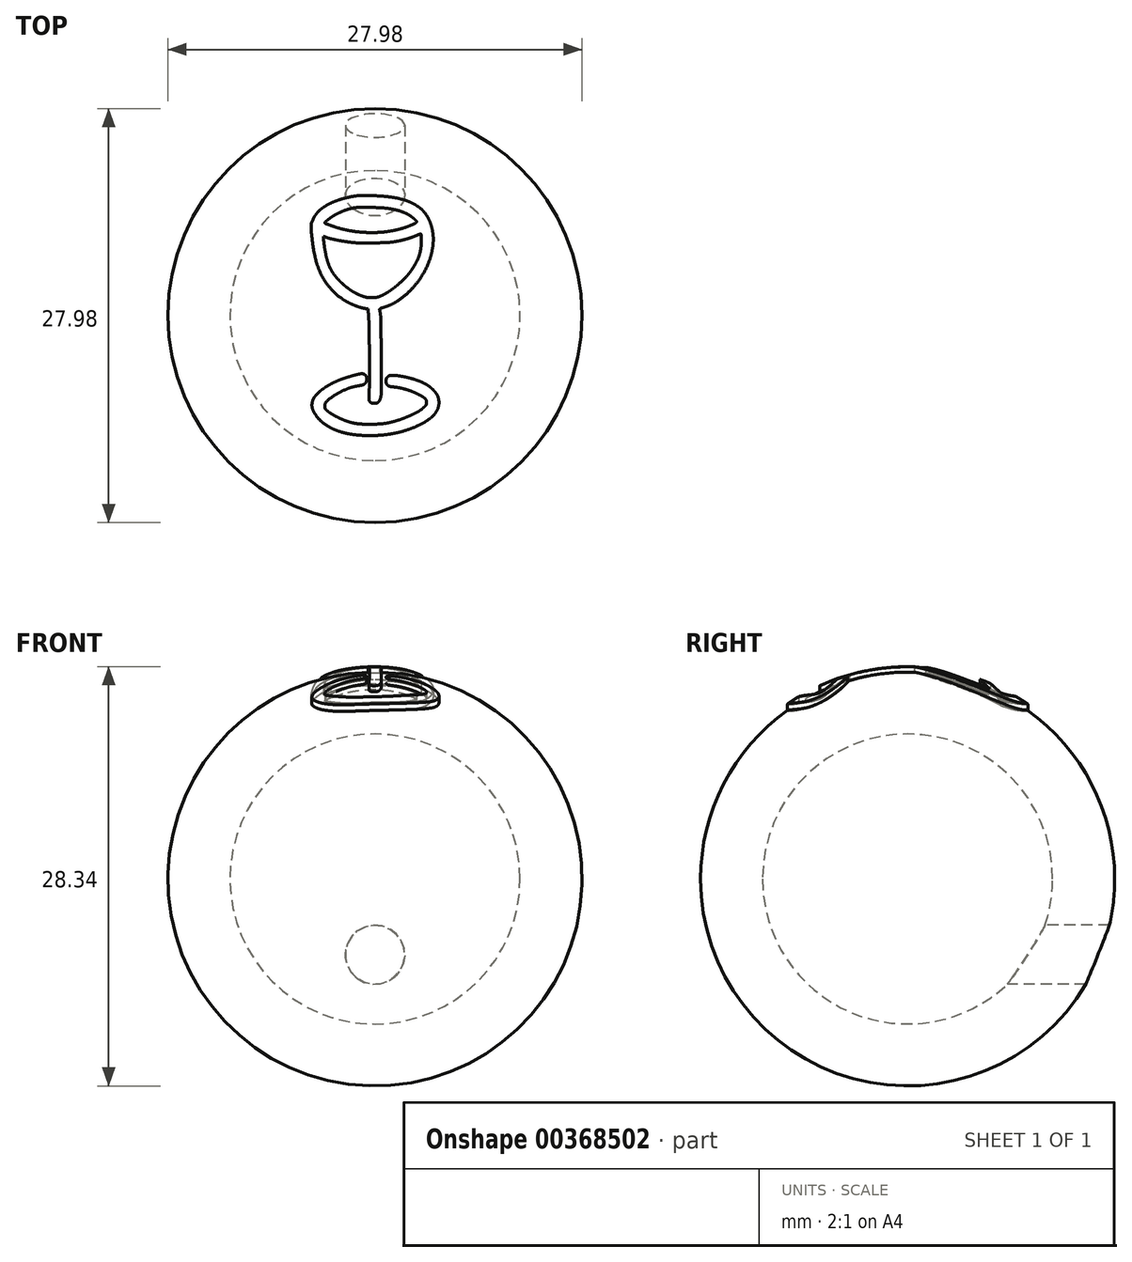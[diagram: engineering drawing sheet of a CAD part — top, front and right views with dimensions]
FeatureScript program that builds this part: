
annotation { "Feature Type Name" : "Feature", "Feature Type Description" : "" }
export const myFeature = defineFeature(function(context is Context, id is Id, definition is map)
    precondition{}
    {
        {
            var Q0;
            Q0=qCreatedBy(makeId("Top.planeOp"),FACE);
            var sketch = newSketch(context, id + "F0", { "sketchPlane" : qUnion([Q0])});
            skLineSegment(sketch, "E0", {"start": v(0, -10) * mm, "end": v(0, 10) * mm});
            skArc(sketch, "E1", {"start": v(0, 10) * mm, "mid": v(-10, 0) * mm, "end": v(0, -10) * mm});
            skSolve(sketch);
        }
        {
            var Q0;
            {var subQ0=sQuery(id+"F0.wireOp",EDGE,"E1");Q0=makeQuery(id+"F0.imprint","IMPRINT",FACE,{"disambiguationData":[TD([[makeQuery(id+"F0.imprint","IMPRINT",EDGE,{"derivedFrom":subQ0}),1.0]])]});}
            var Q1;
            Q1=sQuery(id+"F0.wireOp",EDGE,"E0");
            revolve(context, id + "F1", {"entities" : qUnion([Q0]), "axis" : qUnion([Q1]), "revolveType" : RevolveType.FULL});
        }
        {
            var Q0;
            Q0=makeQuery(id+"F1.opRevolve","SWEPT_BODY",BODY,{"disambiguationData":[OSD([sQuery(id+"F0.wireOp",EDGE,"E0"),sQuery(id+"F0.wireOp",EDGE,"E1")])]});
            var Q1;
            Q1=sQuery(id+"F0.wireOp",VERTEX,"NPe4G0ez-t7S9-9isL-QO5v-uuJu600mHcIT.center");
            var Q2;
            Q2=sQuery(id+"F0.wireOp",VERTEX,"E1.center");
            transform(context, id + "F2", {"entities" : qUnion([Q0]), "transformType" : TransformType.SCALE_UNIFORMLY, "scale" : 33.3, "scalePoint" : qUnion([Q2]), "makeCopy" : false});
        }
        {
            var Q0;
            Q0=qCreatedBy(makeId("Top.planeOp"),FACE);
            var sketch = newSketch(context, id + "F3", { "sketchPlane" : qUnion([Q0])});
            skArc(sketch, "E2", {"start": v(-28, 192.81) * mm, "mid": v(-31.38, 192.4) * mm, "end": v(-34.76, 191.86) * mm});
            skArc(sketch, "E3", {"start": v(-34.76, 191.86) * mm, "mid": v(-38.6, 191.14) * mm, "end": v(-42.43, 190.34) * mm});
            skArc(sketch, "E4", {"start": v(-42.43, 190.34) * mm, "mid": v(-46.3, 189.44) * mm, "end": v(-50.14, 188.46) * mm});
            skArc(sketch, "E5", {"start": v(-50.14, 188.46) * mm, "mid": v(-53.62, 187.47) * mm, "end": v(-57.07, 186.38) * mm});
            skArc(sketch, "E6", {"start": v(-57.07, 186.38) * mm, "mid": v(-64.8, 183.56) * mm, "end": v(-72.35, 180.29) * mm});
            skArc(sketch, "E7", {"start": v(-72.35, 180.29) * mm, "mid": v(-78.57, 177) * mm, "end": v(-84.46, 173.13) * mm});
            skArc(sketch, "E8", {"start": v(-84.46, 173.13) * mm, "mid": v(-89.14, 169.3) * mm, "end": v(-93.37, 164.97) * mm});
            skArc(sketch, "E9", {"start": v(-93.37, 164.97) * mm, "mid": v(-96.59, 160.63) * mm, "end": v(-99.08, 155.83) * mm});
            skArc(sketch, "E10", {"start": v(-99.08, 155.83) * mm, "mid": v(-99.5, 154.83) * mm, "end": v(-99.94, 153.82) * mm});
            skArc(sketch, "E11", {"start": v(-99.94, 153.82) * mm, "mid": v(-100.4, 152.79) * mm, "end": v(-100.85, 151.75) * mm});
            skArc(sketch, "E12", {"start": v(-100.85, 151.75) * mm, "mid": v(-101.26, 150.84) * mm, "end": v(-101.67, 149.92) * mm});
            skArc(sketch, "E13", {"start": v(-101.67, 149.92) * mm, "mid": v(-101.95, 149.32) * mm, "end": v(-102.24, 148.73) * mm});
            skArc(sketch, "E14", {"start": v(-102.24, 148.73) * mm, "mid": v(-102.57, 147.87) * mm, "end": v(-102.73, 146.96) * mm});
            skArc(sketch, "E15", {"start": v(-102.73, 146.96) * mm, "mid": v(-102.82, 145.41) * mm, "end": v(-102.85, 143.86) * mm});
            skArc(sketch, "E16", {"start": v(-102.85, 143.86) * mm, "mid": v(-102.8, 141.6) * mm, "end": v(-102.69, 139.34) * mm});
            skArc(sketch, "E17", {"start": v(-102.69, 139.34) * mm, "mid": v(-102.44, 135.94) * mm, "end": v(-102.17, 132.54) * mm});
            skArc(sketch, "E18", {"start": v(-102.17, 132.54) * mm, "mid": v(-100.04, 114.16) * mm, "end": v(-96.8, 95.94) * mm});
            skArc(sketch, "E19", {"start": v(-96.8, 95.94) * mm, "mid": v(-92.94, 81.56) * mm, "end": v(-87.47, 67.71) * mm});
            skArc(sketch, "E20", {"start": v(-87.47, 67.71) * mm, "mid": v(-81.13, 56.12) * mm, "end": v(-73.3, 45.49) * mm});
            skArc(sketch, "E21", {"start": v(-73.3, 45.49) * mm, "mid": v(-63.92, 35.71) * mm, "end": v(-53.4, 27.18) * mm});
            skArc(sketch, "E22", {"start": v(-53.4, 27.18) * mm, "mid": v(-49.24, 24.41) * mm, "end": v(-44.9, 21.92) * mm});
            skArc(sketch, "E23", {"start": v(-44.9, 21.92) * mm, "mid": v(-39.88, 19.4) * mm, "end": v(-34.74, 17.1) * mm});
            skArc(sketch, "E24", {"start": v(-34.74, 17.1) * mm, "mid": v(-29.55, 15.07) * mm, "end": v(-24.28, 13.28) * mm});
            skArc(sketch, "E25", {"start": v(-24.28, 13.28) * mm, "mid": v(-19.62, 12) * mm, "end": v(-14.89, 11.06) * mm});
            skLineSegment(sketch, "E26", {"start": v(-14.89, 11.06) * mm, "end": v(-11.28, 10.47) * mm});
            skLineSegment(sketch, "E27", {"start": v(-11.28, 10.47) * mm, "end": v(-10.56, 2.24) * mm});
            skArc(sketch, "E28", {"start": v(-10.56, 2.24) * mm, "mid": v(-9.95, -6.44) * mm, "end": v(-9.64, -15.14) * mm});
            skArc(sketch, "E29", {"start": v(-9.64, -15.14) * mm, "mid": v(-9.3, -35.9) * mm, "end": v(-9.02, -56.67) * mm});
            skArc(sketch, "E30", {"start": v(-9.02, -56.67) * mm, "mid": v(-8.82, -77.32) * mm, "end": v(-8.7, -97.97) * mm});
            skArc(sketch, "E31", {"start": v(-8.7, -97.97) * mm, "mid": v(-8.8, -108.17) * mm, "end": v(-9.18, -118.37) * mm});
            skArc(sketch, "E32", {"start": v(-9.18, -118.37) * mm, "mid": v(-9.47, -124.4) * mm, "end": v(-9.74, -130.44) * mm});
            skArc(sketch, "E33", {"start": v(-9.74, -130.44) * mm, "mid": v(-9.78, -132.57) * mm, "end": v(-9.7, -134.7) * mm});
            skArc(sketch, "E34", {"start": v(-9.7, -134.7) * mm, "mid": v(-9.52, -135.94) * mm, "end": v(-9.15, -137.13) * mm});
            skArc(sketch, "E35", {"start": v(-9.15, -137.13) * mm, "mid": v(-8.6, -138.18) * mm, "end": v(-7.87, -139.12) * mm});
            skArc(sketch, "E36", {"start": v(-7.87, -139.12) * mm, "mid": v(-7.27, -139.7) * mm, "end": v(-6.62, -140.22) * mm});
            skArc(sketch, "E37", {"start": v(-6.62, -140.22) * mm, "mid": v(-5.96, -140.63) * mm, "end": v(-5.26, -140.95) * mm});
            skArc(sketch, "E38", {"start": v(-5.26, -140.95) * mm, "mid": v(-4.48, -141.2) * mm, "end": v(-3.68, -141.36) * mm});
            skArc(sketch, "E39", {"start": v(-3.68, -141.36) * mm, "mid": v(-2.72, -141.46) * mm, "end": v(-1.75, -141.5) * mm});
            skArc(sketch, "E40", {"start": v(-1.75, -141.5) * mm, "mid": v(0, -141.42) * mm, "end": v(1.72, -141.18) * mm});
            skArc(sketch, "E41", {"start": v(1.72, -141.18) * mm, "mid": v(3.04, -140.82) * mm, "end": v(4.26, -140.22) * mm});
            skArc(sketch, "E42", {"start": v(4.26, -140.22) * mm, "mid": v(5.31, -139.43) * mm, "end": v(6.2, -138.45) * mm});
            skArc(sketch, "E43", {"start": v(6.2, -138.45) * mm, "mid": v(7.08, -137.1) * mm, "end": v(7.82, -135.66) * mm});
            skArc(sketch, "E44", {"start": v(7.82, -135.66) * mm, "mid": v(9.39, -130.88) * mm, "end": v(9.93, -125.87) * mm});
            skArc(sketch, "E45", {"start": v(9.93, -125.87) * mm, "mid": v(9.97, -95.78) * mm, "end": v(9.93, -65.68) * mm});
            skArc(sketch, "E46", {"start": v(9.93, -65.68) * mm, "mid": v(9.77, -36.7) * mm, "end": v(9.47, -7.73) * mm});
            skArc(sketch, "E47", {"start": v(9.47, -7.73) * mm, "mid": v(8.9, 0.7) * mm, "end": v(7.4, 9) * mm});
            skArc(sketch, "E48", {"start": v(7.4, 9) * mm, "mid": v(7.35, 9.57) * mm, "end": v(7.47, 10.13) * mm});
            skArc(sketch, "E49", {"start": v(7.47, 10.13) * mm, "mid": v(7.75, 10.61) * mm, "end": v(8.17, 10.99) * mm});
            skArc(sketch, "E50", {"start": v(8.17, 10.99) * mm, "mid": v(8.98, 11.43) * mm, "end": v(9.85, 11.77) * mm});
            skArc(sketch, "E51", {"start": v(9.85, 11.77) * mm, "mid": v(11.67, 12.35) * mm, "end": v(13.5, 12.9) * mm});
            skArc(sketch, "E52", {"start": v(13.5, 12.9) * mm, "mid": v(25.53, 17.38) * mm, "end": v(36.7, 23.67) * mm});
            skArc(sketch, "E53", {"start": v(36.7, 23.67) * mm, "mid": v(48.2, 32.34) * mm, "end": v(58.64, 42.23) * mm});
            skArc(sketch, "E54", {"start": v(58.64, 42.23) * mm, "mid": v(68.36, 53.67) * mm, "end": v(76.8, 66.08) * mm});
            skArc(sketch, "E55", {"start": v(76.8, 66.08) * mm, "mid": v(83.57, 78.94) * mm, "end": v(88.8, 92.5) * mm});
            skArc(sketch, "E56", {"start": v(88.8, 92.5) * mm, "mid": v(91.23, 101.41) * mm, "end": v(92.9, 110.5) * mm});
            skArc(sketch, "E57", {"start": v(92.9, 110.5) * mm, "mid": v(93.67, 119.1) * mm, "end": v(93.55, 127.73) * mm});
            skArc(sketch, "E58", {"start": v(93.55, 127.73) * mm, "mid": v(92.56, 135.93) * mm, "end": v(90.68, 143.97) * mm});
            skArc(sketch, "E59", {"start": v(90.68, 143.97) * mm, "mid": v(87.96, 151.66) * mm, "end": v(84.4, 159) * mm});
            skArc(sketch, "E60", {"start": v(84.4, 159) * mm, "mid": v(80.6, 164.75) * mm, "end": v(75.97, 169.86) * mm});
            skArc(sketch, "E61", {"start": v(75.97, 169.86) * mm, "mid": v(70.26, 174.63) * mm, "end": v(64.02, 178.68) * mm});
            skArc(sketch, "E62", {"start": v(64.02, 178.68) * mm, "mid": v(56.48, 182.45) * mm, "end": v(48.6, 185.4) * mm});
            skArc(sketch, "E63", {"start": v(48.6, 185.4) * mm, "mid": v(39.26, 188) * mm, "end": v(29.76, 189.95) * mm});
            skArc(sketch, "E64", {"start": v(29.76, 189.95) * mm, "mid": v(23.24, 190.92) * mm, "end": v(16.69, 191.62) * mm});
            skArc(sketch, "E65", {"start": v(16.69, 191.62) * mm, "mid": v(8.13, 192.28) * mm, "end": v(-0.44, 192.79) * mm});
            skArc(sketch, "E66", {"start": v(-0.44, 192.79) * mm, "mid": v(-8.76, 193.13) * mm, "end": v(-17.1, 193.32) * mm});
            skArc(sketch, "E67", {"start": v(-17.1, 193.32) * mm, "mid": v(-22.55, 193.23) * mm, "end": v(-28, 192.81) * mm});
            skArc(sketch, "E68", {"start": v(23, 172) * mm, "mid": v(27.27, 171.24) * mm, "end": v(31.52, 170.4) * mm});
            skArc(sketch, "E69", {"start": v(31.52, 170.4) * mm, "mid": v(34.9, 169.63) * mm, "end": v(38.25, 168.73) * mm});
            skArc(sketch, "E70", {"start": v(38.25, 168.73) * mm, "mid": v(41.28, 167.77) * mm, "end": v(44.27, 166.68) * mm});
            skArc(sketch, "E71", {"start": v(44.27, 166.68) * mm, "mid": v(47.43, 165.38) * mm, "end": v(50.56, 163.97) * mm});
            skArc(sketch, "E72", {"start": v(50.56, 163.97) * mm, "mid": v(53.44, 162.47) * mm, "end": v(56.2, 160.78) * mm});
            skArc(sketch, "E73", {"start": v(56.2, 160.78) * mm, "mid": v(59.05, 158.78) * mm, "end": v(61.78, 156.62) * mm});
            skArc(sketch, "E74", {"start": v(61.78, 156.62) * mm, "mid": v(64.08, 154.6) * mm, "end": v(66.28, 152.48) * mm});
            skArc(sketch, "E75", {"start": v(66.28, 152.48) * mm, "mid": v(66.84, 151.48) * mm, "end": v(66.79, 150.33) * mm});
            skArc(sketch, "E76", {"start": v(66.79, 150.33) * mm, "mid": v(66.12, 149.19) * mm, "end": v(65.05, 148.41) * mm});
            skArc(sketch, "E77", {"start": v(65.05, 148.41) * mm, "mid": v(60.8, 146.55) * mm, "end": v(56.5, 144.76) * mm});
            skArc(sketch, "E78", {"start": v(56.5, 144.76) * mm, "mid": v(51.74, 142.91) * mm, "end": v(46.93, 141.22) * mm});
            skArc(sketch, "E79", {"start": v(46.93, 141.22) * mm, "mid": v(42.34, 139.79) * mm, "end": v(37.7, 138.53) * mm});
            skArc(sketch, "E80", {"start": v(37.7, 138.53) * mm, "mid": v(24.83, 135.84) * mm, "end": v(11.79, 134.2) * mm});
            skArc(sketch, "E81", {"start": v(11.79, 134.2) * mm, "mid": v(-2.07, 133.48) * mm, "end": v(-15.94, 133.71) * mm});
            skArc(sketch, "E82", {"start": v(-15.94, 133.71) * mm, "mid": v(-29.73, 134.9) * mm, "end": v(-43.4, 137.01) * mm});
            skArc(sketch, "E83", {"start": v(-43.4, 137.01) * mm, "mid": v(-56.09, 139.97) * mm, "end": v(-68.5, 143.96) * mm});
            skArc(sketch, "E84", {"start": v(-68.5, 143.96) * mm, "mid": v(-70.45, 144.68) * mm, "end": v(-72.41, 145.4) * mm});
            skArc(sketch, "E85", {"start": v(-72.41, 145.4) * mm, "mid": v(-74.17, 146.03) * mm, "end": v(-75.92, 146.67) * mm});
            skArc(sketch, "E86", {"start": v(-75.92, 146.67) * mm, "mid": v(-77.4, 147.2) * mm, "end": v(-78.88, 147.74) * mm});
            skArc(sketch, "E87", {"start": v(-78.88, 147.74) * mm, "mid": v(-79.3, 147.9) * mm, "end": v(-79.74, 148.04) * mm});
            skArc(sketch, "E88", {"start": v(-79.74, 148.04) * mm, "mid": v(-80.25, 148.32) * mm, "end": v(-80.62, 148.77) * mm});
            skArc(sketch, "E89", {"start": v(-80.62, 148.77) * mm, "mid": v(-80.74, 149.28) * mm, "end": v(-80.58, 149.77) * mm});
            skArc(sketch, "E90", {"start": v(-80.58, 149.77) * mm, "mid": v(-79.94, 150.6) * mm, "end": v(-79.2, 151.33) * mm});
            skArc(sketch, "E91", {"start": v(-79.2, 151.33) * mm, "mid": v(-77.48, 152.74) * mm, "end": v(-75.74, 154.13) * mm});
            skArc(sketch, "E92", {"start": v(-75.74, 154.13) * mm, "mid": v(-70.76, 157.76) * mm, "end": v(-65.57, 161.08) * mm});
            skArc(sketch, "E93", {"start": v(-65.57, 161.08) * mm, "mid": v(-60.08, 164.12) * mm, "end": v(-54.43, 166.82) * mm});
            skArc(sketch, "E94", {"start": v(-54.43, 166.82) * mm, "mid": v(-48.77, 169.12) * mm, "end": v(-43, 171.06) * mm});
            skArc(sketch, "E95", {"start": v(-43, 171.06) * mm, "mid": v(-37.5, 172.49) * mm, "end": v(-31.93, 173.5) * mm});
            skArc(sketch, "E96", {"start": v(-31.93, 173.5) * mm, "mid": v(-27.17, 174) * mm, "end": v(-22.38, 174.16) * mm});
            skArc(sketch, "E97", {"start": v(-22.38, 174.16) * mm, "mid": v(-13.79, 174.1) * mm, "end": v(-5.2, 173.93) * mm});
            skArc(sketch, "E98", {"start": v(-5.2, 173.93) * mm, "mid": v(3.46, 173.63) * mm, "end": v(12.1, 173.2) * mm});
            skArc(sketch, "E99", {"start": v(12.1, 173.2) * mm, "mid": v(17.57, 172.75) * mm, "end": v(23, 172) * mm});
            skArc(sketch, "E100", {"start": v(74.45, 118.91) * mm, "mid": v(74.2, 112.9) * mm, "end": v(73.54, 106.92) * mm});
            skArc(sketch, "E101", {"start": v(73.54, 106.92) * mm, "mid": v(72.47, 101.46) * mm, "end": v(70.92, 96.12) * mm});
            skArc(sketch, "E102", {"start": v(70.92, 96.12) * mm, "mid": v(68.79, 90.64) * mm, "end": v(66.2, 85.35) * mm});
            skArc(sketch, "E103", {"start": v(66.2, 85.35) * mm, "mid": v(62.73, 79.3) * mm, "end": v(58.94, 73.4) * mm});
            skArc(sketch, "E104", {"start": v(58.94, 73.4) * mm, "mid": v(54.72, 67.67) * mm, "end": v(50.07, 62.26) * mm});
            skArc(sketch, "E105", {"start": v(50.07, 62.26) * mm, "mid": v(44.37, 56.43) * mm, "end": v(38.38, 50.9) * mm});
            skArc(sketch, "E106", {"start": v(38.38, 50.9) * mm, "mid": v(32.1, 45.67) * mm, "end": v(25.56, 40.76) * mm});
            skArc(sketch, "E107", {"start": v(25.56, 40.76) * mm, "mid": v(19.56, 36.81) * mm, "end": v(13.27, 33.33) * mm});
            skArc(sketch, "E108", {"start": v(13.27, 33.33) * mm, "mid": v(10.86, 32.14) * mm, "end": v(8.43, 31.02) * mm});
            skArc(sketch, "E109", {"start": v(8.43, 31.02) * mm, "mid": v(6.75, 30.34) * mm, "end": v(5.03, 29.79) * mm});
            skArc(sketch, "E110", {"start": v(5.03, 29.79) * mm, "mid": v(3.33, 29.38) * mm, "end": v(1.6, 29.12) * mm});
            skArc(sketch, "E111", {"start": v(1.6, 29.12) * mm, "mid": v(-0.81, 28.88) * mm, "end": v(-3.23, 28.72) * mm});
            skArc(sketch, "E112", {"start": v(-3.23, 28.72) * mm, "mid": v(-5.59, 28.63) * mm, "end": v(-7.95, 28.6) * mm});
            skArc(sketch, "E113", {"start": v(-7.95, 28.6) * mm, "mid": v(-9.7, 28.66) * mm, "end": v(-11.43, 28.84) * mm});
            skArc(sketch, "E114", {"start": v(-11.43, 28.84) * mm, "mid": v(-13.15, 29.14) * mm, "end": v(-14.86, 29.55) * mm});
            skArc(sketch, "E115", {"start": v(-14.86, 29.55) * mm, "mid": v(-17.14, 30.22) * mm, "end": v(-19.4, 30.94) * mm});
            skArc(sketch, "E116", {"start": v(-19.4, 30.94) * mm, "mid": v(-24.3, 32.77) * mm, "end": v(-29.04, 34.94) * mm});
            skArc(sketch, "E117", {"start": v(-29.04, 34.94) * mm, "mid": v(-33.85, 37.5) * mm, "end": v(-38.48, 40.37) * mm});
            skArc(sketch, "E118", {"start": v(-38.48, 40.37) * mm, "mid": v(-43.29, 43.72) * mm, "end": v(-47.9, 47.34) * mm});
            skArc(sketch, "E119", {"start": v(-47.9, 47.34) * mm, "mid": v(-52.76, 51.57) * mm, "end": v(-57.44, 56) * mm});
            skArc(sketch, "E120", {"start": v(-57.44, 56) * mm, "mid": v(-62.23, 61.17) * mm, "end": v(-66.53, 66.76) * mm});
            skArc(sketch, "E121", {"start": v(-66.53, 66.76) * mm, "mid": v(-70.15, 72.57) * mm, "end": v(-73.17, 78.7) * mm});
            skArc(sketch, "E122", {"start": v(-73.17, 78.7) * mm, "mid": v(-75.9, 85.84) * mm, "end": v(-77.98, 93.19) * mm});
            skArc(sketch, "E123", {"start": v(-77.98, 93.19) * mm, "mid": v(-79.95, 102.45) * mm, "end": v(-81.5, 111.79) * mm});
            skArc(sketch, "E124", {"start": v(-81.5, 111.79) * mm, "mid": v(-81.79, 113.84) * mm, "end": v(-82.06, 115.9) * mm});
            skArc(sketch, "E125", {"start": v(-82.06, 115.9) * mm, "mid": v(-82.3, 117.84) * mm, "end": v(-82.53, 119.8) * mm});
            skArc(sketch, "E126", {"start": v(-82.53, 119.8) * mm, "mid": v(-82.72, 121.44) * mm, "end": v(-82.89, 123.1) * mm});
            skArc(sketch, "E127", {"start": v(-82.89, 123.1) * mm, "mid": v(-82.95, 123.9) * mm, "end": v(-82.97, 124.7) * mm});
            skLineSegment(sketch, "E128", {"start": v(-82.97, 124.7) * mm, "end": v(-83, 127.4) * mm});
            skLineSegment(sketch, "E129", {"start": v(-83, 127.4) * mm, "end": v(-77.24, 125.41) * mm});
            skArc(sketch, "E130", {"start": v(-77.24, 125.41) * mm, "mid": v(-73.46, 124.22) * mm, "end": v(-69.61, 123.22) * mm});
            skArc(sketch, "E131", {"start": v(-69.61, 123.22) * mm, "mid": v(-64.09, 122) * mm, "end": v(-58.54, 120.88) * mm});
            skArc(sketch, "E132", {"start": v(-58.54, 120.88) * mm, "mid": v(-52.55, 119.8) * mm, "end": v(-46.55, 118.82) * mm});
            skArc(sketch, "E133", {"start": v(-46.55, 118.82) * mm, "mid": v(-41.1, 118.06) * mm, "end": v(-35.66, 117.44) * mm});
            skArc(sketch, "E134", {"start": v(-35.66, 117.44) * mm, "mid": v(-28.26, 116.87) * mm, "end": v(-20.84, 116.63) * mm});
            skArc(sketch, "E135", {"start": v(-20.84, 116.63) * mm, "mid": v(-10.4, 116.6) * mm, "end": v(0.05, 116.76) * mm});
            skArc(sketch, "E136", {"start": v(0.05, 116.76) * mm, "mid": v(10.3, 117.07) * mm, "end": v(20.54, 117.54) * mm});
            skArc(sketch, "E137", {"start": v(20.54, 117.54) * mm, "mid": v(26.8, 118.08) * mm, "end": v(33, 119) * mm});
            skArc(sketch, "E138", {"start": v(33, 119) * mm, "mid": v(37.48, 119.88) * mm, "end": v(41.92, 120.86) * mm});
            skArc(sketch, "E139", {"start": v(41.92, 120.86) * mm, "mid": v(46.33, 121.94) * mm, "end": v(50.71, 123.15) * mm});
            skArc(sketch, "E140", {"start": v(50.71, 123.15) * mm, "mid": v(54.81, 124.38) * mm, "end": v(58.87, 125.73) * mm});
            skArc(sketch, "E141", {"start": v(58.87, 125.73) * mm, "mid": v(62.4, 127.02) * mm, "end": v(65.87, 128.45) * mm});
            skArc(sketch, "E142", {"start": v(65.87, 128.45) * mm, "mid": v(67.17, 129.01) * mm, "end": v(68.48, 129.54) * mm});
            skArc(sketch, "E143", {"start": v(68.48, 129.54) * mm, "mid": v(69.66, 130) * mm, "end": v(70.85, 130.42) * mm});
            skArc(sketch, "E144", {"start": v(70.85, 130.42) * mm, "mid": v(71.84, 130.75) * mm, "end": v(72.84, 131.07) * mm});
            skArc(sketch, "E145", {"start": v(72.84, 131.07) * mm, "mid": v(73.17, 131.13) * mm, "end": v(73.5, 131.09) * mm});
            skArc(sketch, "E146", {"start": v(73.5, 131.09) * mm, "mid": v(73.8, 130.9) * mm, "end": v(73.94, 130.6) * mm});
            skArc(sketch, "E147", {"start": v(73.94, 130.6) * mm, "mid": v(74.09, 129.1) * mm, "end": v(74.22, 127.62) * mm});
            skArc(sketch, "E148", {"start": v(74.22, 127.62) * mm, "mid": v(74.34, 125.7) * mm, "end": v(74.4, 123.79) * mm});
            skArc(sketch, "E149", {"start": v(74.4, 123.79) * mm, "mid": v(74.45, 121.35) * mm, "end": v(74.45, 118.91) * mm});
            skArc(sketch, "E150", {"start": v(-34.65, -96.5) * mm, "mid": v(-43.47, -99) * mm, "end": v(-52.16, -101.92) * mm});
            skArc(sketch, "E151", {"start": v(-52.16, -101.92) * mm, "mid": v(-60, -105) * mm, "end": v(-67.65, -108.52) * mm});
            skArc(sketch, "E152", {"start": v(-67.65, -108.52) * mm, "mid": v(-74.33, -112.1) * mm, "end": v(-80.77, -116.1) * mm});
            skArc(sketch, "E153", {"start": v(-80.77, -116.1) * mm, "mid": v(-86.14, -120.06) * mm, "end": v(-91.13, -124.5) * mm});
            skArc(sketch, "E154", {"start": v(-91.13, -124.5) * mm, "mid": v(-93.26, -126.63) * mm, "end": v(-95.35, -128.8) * mm});
            skArc(sketch, "E155", {"start": v(-95.35, -128.8) * mm, "mid": v(-96.6, -130.2) * mm, "end": v(-97.73, -131.7) * mm});
            skArc(sketch, "E156", {"start": v(-97.73, -131.7) * mm, "mid": v(-98.56, -133.01) * mm, "end": v(-99.25, -134.4) * mm});
            skArc(sketch, "E157", {"start": v(-99.25, -134.4) * mm, "mid": v(-99.92, -136.08) * mm, "end": v(-100.48, -137.8) * mm});
            skArc(sketch, "E158", {"start": v(-100.48, -137.8) * mm, "mid": v(-101.1, -140.5) * mm, "end": v(-101.43, -143.24) * mm});
            skArc(sketch, "E159", {"start": v(-101.43, -143.24) * mm, "mid": v(-101.41, -145.8) * mm, "end": v(-101.04, -148.34) * mm});
            skArc(sketch, "E160", {"start": v(-101.04, -148.34) * mm, "mid": v(-100.3, -151.03) * mm, "end": v(-99.22, -153.6) * mm});
            skArc(sketch, "E161", {"start": v(-99.22, -153.6) * mm, "mid": v(-97.61, -156.62) * mm, "end": v(-95.8, -159.53) * mm});
            skArc(sketch, "E162", {"start": v(-95.8, -159.53) * mm, "mid": v(-89.92, -166.94) * mm, "end": v(-82.9, -173.28) * mm});
            skArc(sketch, "E163", {"start": v(-82.9, -173.28) * mm, "mid": v(-74.32, -179.02) * mm, "end": v(-65.07, -183.62) * mm});
            skArc(sketch, "E164", {"start": v(-65.07, -183.62) * mm, "mid": v(-54.02, -187.58) * mm, "end": v(-42.6, -190.32) * mm});
            skArc(sketch, "E165", {"start": v(-42.6, -190.32) * mm, "mid": v(-29.29, -192.24) * mm, "end": v(-15.88, -193.2) * mm});
            skArc(sketch, "E166", {"start": v(-15.88, -193.2) * mm, "mid": v(-3.6, -193.28) * mm, "end": v(8.67, -192.7) * mm});
            skArc(sketch, "E167", {"start": v(8.67, -192.7) * mm, "mid": v(20.3, -191.45) * mm, "end": v(31.83, -189.47) * mm});
            skArc(sketch, "E168", {"start": v(31.83, -189.47) * mm, "mid": v(42.82, -186.85) * mm, "end": v(53.62, -183.51) * mm});
            skArc(sketch, "E169", {"start": v(53.62, -183.51) * mm, "mid": v(64, -179.52) * mm, "end": v(74.07, -174.83) * mm});
            skArc(sketch, "E170", {"start": v(74.07, -174.83) * mm, "mid": v(81.9, -170.36) * mm, "end": v(89.25, -165.16) * mm});
            skArc(sketch, "E171", {"start": v(89.25, -165.16) * mm, "mid": v(94.55, -160.17) * mm, "end": v(98.88, -154.31) * mm});
            skArc(sketch, "E172", {"start": v(98.88, -154.31) * mm, "mid": v(101.48, -148.67) * mm, "end": v(102.73, -142.58) * mm});
            skArc(sketch, "E173", {"start": v(102.73, -142.58) * mm, "mid": v(102.6, -136.36) * mm, "end": v(101.06, -130.32) * mm});
            skArc(sketch, "E174", {"start": v(101.06, -130.32) * mm, "mid": v(99.8, -127.56) * mm, "end": v(98.15, -125) * mm});
            skArc(sketch, "E175", {"start": v(98.15, -125) * mm, "mid": v(95.8, -122.07) * mm, "end": v(93.23, -119.32) * mm});
            skArc(sketch, "E176", {"start": v(93.23, -119.32) * mm, "mid": v(90.25, -116.55) * mm, "end": v(87.08, -114) * mm});
            skArc(sketch, "E177", {"start": v(87.08, -114) * mm, "mid": v(83.81, -111.76) * mm, "end": v(80.39, -109.77) * mm});
            skArc(sketch, "E178", {"start": v(80.39, -109.77) * mm, "mid": v(74.8, -107.06) * mm, "end": v(69.03, -104.76) * mm});
            skArc(sketch, "E179", {"start": v(69.03, -104.76) * mm, "mid": v(62.06, -102.45) * mm, "end": v(55, -100.46) * mm});
            skArc(sketch, "E180", {"start": v(55, -100.46) * mm, "mid": v(47.95, -98.8) * mm, "end": v(40.82, -97.46) * mm});
            skArc(sketch, "E181", {"start": v(40.82, -97.46) * mm, "mid": v(34.96, -96.74) * mm, "end": v(29.05, -96.5) * mm});
            skArc(sketch, "E182", {"start": v(29.05, -96.5) * mm, "mid": v(27.14, -96.52) * mm, "end": v(25.23, -96.58) * mm});
            skArc(sketch, "E183", {"start": v(25.23, -96.58) * mm, "mid": v(24.15, -96.7) * mm, "end": v(23.09, -96.93) * mm});
            skArc(sketch, "E184", {"start": v(23.09, -96.93) * mm, "mid": v(22.28, -97.24) * mm, "end": v(21.53, -97.68) * mm});
            skArc(sketch, "E185", {"start": v(21.53, -97.68) * mm, "mid": v(20.7, -98.32) * mm, "end": v(19.96, -99.05) * mm});
            skArc(sketch, "E186", {"start": v(19.96, -99.05) * mm, "mid": v(18.9, -100.41) * mm, "end": v(18.15, -101.96) * mm});
            skArc(sketch, "E187", {"start": v(18.15, -101.96) * mm, "mid": v(17.67, -103.68) * mm, "end": v(17.5, -105.46) * mm});
            skArc(sketch, "E188", {"start": v(17.5, -105.46) * mm, "mid": v(17.64, -107.23) * mm, "end": v(18.1, -108.95) * mm});
            skArc(sketch, "E189", {"start": v(18.1, -108.95) * mm, "mid": v(18.82, -110.48) * mm, "end": v(19.85, -111.83) * mm});
            skArc(sketch, "E190", {"start": v(19.85, -111.83) * mm, "mid": v(20.58, -112.51) * mm, "end": v(21.4, -113.1) * mm});
            skArc(sketch, "E191", {"start": v(21.4, -113.1) * mm, "mid": v(22.26, -113.58) * mm, "end": v(23.18, -113.94) * mm});
            skArc(sketch, "E192", {"start": v(23.18, -113.94) * mm, "mid": v(24.43, -114.28) * mm, "end": v(25.7, -114.51) * mm});
            skArc(sketch, "E193", {"start": v(25.7, -114.51) * mm, "mid": v(27.76, -114.77) * mm, "end": v(29.83, -114.99) * mm});
            skArc(sketch, "E194", {"start": v(29.83, -114.99) * mm, "mid": v(34.38, -115.52) * mm, "end": v(38.9, -116.3) * mm});
            skArc(sketch, "E195", {"start": v(38.9, -116.3) * mm, "mid": v(43.66, -117.33) * mm, "end": v(48.37, -118.56) * mm});
            skArc(sketch, "E196", {"start": v(48.37, -118.56) * mm, "mid": v(53.13, -120.02) * mm, "end": v(57.83, -121.68) * mm});
            skArc(sketch, "E197", {"start": v(57.83, -121.68) * mm, "mid": v(62.38, -123.5) * mm, "end": v(66.85, -125.51) * mm});
            skArc(sketch, "E198", {"start": v(66.85, -125.51) * mm, "mid": v(71.1, -127.61) * mm, "end": v(75.29, -129.81) * mm});
            skArc(sketch, "E199", {"start": v(75.29, -129.81) * mm, "mid": v(77.66, -131.27) * mm, "end": v(79.85, -133) * mm});
            skArc(sketch, "E200", {"start": v(79.85, -133) * mm, "mid": v(81.17, -134.41) * mm, "end": v(82.18, -136.07) * mm});
            skArc(sketch, "E201", {"start": v(82.18, -136.07) * mm, "mid": v(82.8, -137.85) * mm, "end": v(83, -139.72) * mm});
            skArc(sketch, "E202", {"start": v(83, -139.72) * mm, "mid": v(82.96, -140.83) * mm, "end": v(82.8, -141.93) * mm});
            skArc(sketch, "E203", {"start": v(82.8, -141.93) * mm, "mid": v(82.56, -142.82) * mm, "end": v(82.18, -143.67) * mm});
            skArc(sketch, "E204", {"start": v(82.18, -143.67) * mm, "mid": v(81.6, -144.6) * mm, "end": v(80.91, -145.45) * mm});
            skArc(sketch, "E205", {"start": v(80.91, -145.45) * mm, "mid": v(79.73, -146.72) * mm, "end": v(78.5, -147.95) * mm});
            skArc(sketch, "E206", {"start": v(78.5, -147.95) * mm, "mid": v(74.22, -151.58) * mm, "end": v(69.49, -154.6) * mm});
            skArc(sketch, "E207", {"start": v(69.49, -154.6) * mm, "mid": v(62.23, -158.37) * mm, "end": v(54.81, -161.8) * mm});
            skArc(sketch, "E208", {"start": v(54.81, -161.8) * mm, "mid": v(46.47, -165.2) * mm, "end": v(37.99, -168.23) * mm});
            skArc(sketch, "E209", {"start": v(37.99, -168.23) * mm, "mid": v(29.88, -170.67) * mm, "end": v(21.66, -172.67) * mm});
            skArc(sketch, "E210", {"start": v(21.66, -172.67) * mm, "mid": v(15.6, -173.75) * mm, "end": v(9.47, -174.4) * mm});
            skArc(sketch, "E211", {"start": v(9.47, -174.4) * mm, "mid": v(1.44, -174.86) * mm, "end": v(-6.6, -175.06) * mm});
            skArc(sketch, "E212", {"start": v(-6.6, -175.06) * mm, "mid": v(-14.57, -175) * mm, "end": v(-22.52, -174.7) * mm});
            skArc(sketch, "E213", {"start": v(-22.52, -174.7) * mm, "mid": v(-28.28, -174.16) * mm, "end": v(-33.98, -173.17) * mm});
            skArc(sketch, "E214", {"start": v(-33.98, -173.17) * mm, "mid": v(-42.09, -171.07) * mm, "end": v(-50, -168.32) * mm});
            skArc(sketch, "E215", {"start": v(-50, -168.32) * mm, "mid": v(-57.95, -164.86) * mm, "end": v(-65.6, -160.83) * mm});
            skArc(sketch, "E216", {"start": v(-65.6, -160.83) * mm, "mid": v(-71.87, -156.93) * mm, "end": v(-77.84, -152.6) * mm});
            skArc(sketch, "E217", {"start": v(-77.84, -152.6) * mm, "mid": v(-80.16, -149.75) * mm, "end": v(-81, -146.16) * mm});
            skArc(sketch, "E218", {"start": v(-81, -146.16) * mm, "mid": v(-79.94, -141.3) * mm, "end": v(-76.96, -137.33) * mm});
            skArc(sketch, "E219", {"start": v(-76.96, -137.33) * mm, "mid": v(-70, -131.79) * mm, "end": v(-62.58, -126.88) * mm});
            skArc(sketch, "E220", {"start": v(-62.58, -126.88) * mm, "mid": v(-53.6, -121.99) * mm, "end": v(-44.23, -117.89) * mm});
            skArc(sketch, "E221", {"start": v(-44.23, -117.89) * mm, "mid": v(-35.24, -114.97) * mm, "end": v(-26, -113.05) * mm});
            skArc(sketch, "E222", {"start": v(-26, -113.05) * mm, "mid": v(-23.72, -112.66) * mm, "end": v(-21.46, -112.16) * mm});
            skArc(sketch, "E223", {"start": v(-21.46, -112.16) * mm, "mid": v(-19.83, -111.67) * mm, "end": v(-18.26, -111) * mm});
            skArc(sketch, "E224", {"start": v(-18.26, -111) * mm, "mid": v(-17.07, -110.31) * mm, "end": v(-16, -109.46) * mm});
            skArc(sketch, "E225", {"start": v(-16, -109.46) * mm, "mid": v(-15.14, -108.5) * mm, "end": v(-14.44, -107.4) * mm});
            skArc(sketch, "E226", {"start": v(-14.44, -107.4) * mm, "mid": v(-13.76, -105.86) * mm, "end": v(-13.28, -104.24) * mm});
            skArc(sketch, "E227", {"start": v(-13.28, -104.24) * mm, "mid": v(-13.05, -102.7) * mm, "end": v(-13.06, -101.14) * mm});
            skArc(sketch, "E228", {"start": v(-13.06, -101.14) * mm, "mid": v(-13.3, -99.7) * mm, "end": v(-13.8, -98.31) * mm});
            skArc(sketch, "E229", {"start": v(-13.8, -98.31) * mm, "mid": v(-14.52, -97.06) * mm, "end": v(-15.45, -95.95) * mm});
            skArc(sketch, "E230", {"start": v(-15.45, -95.95) * mm, "mid": v(-16.65, -94.96) * mm, "end": v(-18.03, -94.24) * mm});
            skArc(sketch, "E231", {"start": v(-18.03, -94.24) * mm, "mid": v(-19.5, -93.8) * mm, "end": v(-21.04, -93.7) * mm});
            skArc(sketch, "E232", {"start": v(-21.04, -93.7) * mm, "mid": v(-23.35, -93.87) * mm, "end": v(-25.63, -94.28) * mm});
            skArc(sketch, "E233", {"start": v(-25.63, -94.28) * mm, "mid": v(-30.15, -95.35) * mm, "end": v(-34.65, -96.5) * mm});
            skArc(sketch, "E234", {"start": v(46.5, 109.42) * mm, "mid": v(40.62, 107.91) * mm, "end": v(34.69, 106.57) * mm});
            skArc(sketch, "E235", {"start": v(34.69, 106.57) * mm, "mid": v(29.15, 105.5) * mm, "end": v(23.57, 104.64) * mm});
            skArc(sketch, "E236", {"start": v(23.57, 104.64) * mm, "mid": v(17.7, 103.94) * mm, "end": v(11.79, 103.43) * mm});
            skArc(sketch, "E237", {"start": v(11.79, 103.43) * mm, "mid": v(4.84, 103.03) * mm, "end": v(-2.12, 102.78) * mm});
            skArc(sketch, "E238", {"start": v(-2.12, 102.78) * mm, "mid": v(-9.27, 102.65) * mm, "end": v(-16.41, 102.65) * mm});
            skArc(sketch, "E239", {"start": v(-16.41, 102.65) * mm, "mid": v(-22.2, 102.8) * mm, "end": v(-28, 103.15) * mm});
            skArc(sketch, "E240", {"start": v(-28, 103.15) * mm, "mid": v(-33.66, 103.68) * mm, "end": v(-39.3, 104.4) * mm});
            skArc(sketch, "E241", {"start": v(-39.3, 104.4) * mm, "mid": v(-46.04, 105.44) * mm, "end": v(-52.75, 106.63) * mm});
            skArc(sketch, "E242", {"start": v(-52.75, 106.63) * mm, "mid": v(-56.1, 107.24) * mm, "end": v(-59.46, 107.82) * mm});
            skArc(sketch, "E243", {"start": v(-59.46, 107.82) * mm, "mid": v(-61.02, 108.03) * mm, "end": v(-62.6, 108.15) * mm});
            skArc(sketch, "E244", {"start": v(-62.6, 108.15) * mm, "mid": v(-63.62, 108.12) * mm, "end": v(-64.62, 107.94) * mm});
            skArc(sketch, "E245", {"start": v(-64.62, 107.94) * mm, "mid": v(-65.53, 107.63) * mm, "end": v(-66.38, 107.17) * mm});
            skArc(sketch, "E246", {"start": v(-66.38, 107.17) * mm, "mid": v(-67.47, 106.28) * mm, "end": v(-68.35, 105.2) * mm});
            skArc(sketch, "E247", {"start": v(-68.35, 105.2) * mm, "mid": v(-68.99, 103.94) * mm, "end": v(-69.35, 102.58) * mm});
            skArc(sketch, "E248", {"start": v(-69.35, 102.58) * mm, "mid": v(-69.51, 100.78) * mm, "end": v(-69.41, 98.99) * mm});
            skArc(sketch, "E249", {"start": v(-69.41, 98.99) * mm, "mid": v(-69.03, 96.45) * mm, "end": v(-68.51, 93.93) * mm});
            skArc(sketch, "E250", {"start": v(-68.51, 93.93) * mm, "mid": v(-65.52, 84.43) * mm, "end": v(-61.12, 75.5) * mm});
            skArc(sketch, "E251", {"start": v(-61.12, 75.5) * mm, "mid": v(-55.22, 66.9) * mm, "end": v(-48.23, 59.16) * mm});
            skArc(sketch, "E252", {"start": v(-48.23, 59.16) * mm, "mid": v(-40.25, 52.4) * mm, "end": v(-31.44, 46.78) * mm});
            skArc(sketch, "E253", {"start": v(-31.44, 46.78) * mm, "mid": v(-22.3, 42.62) * mm, "end": v(-12.64, 39.88) * mm});
            skArc(sketch, "E254", {"start": v(-12.64, 39.88) * mm, "mid": v(-8.94, 39.25) * mm, "end": v(-5.2, 38.86) * mm});
            skArc(sketch, "E255", {"start": v(-5.2, 38.86) * mm, "mid": v(-2.07, 38.8) * mm, "end": v(1.05, 39.1) * mm});
            skArc(sketch, "E256", {"start": v(1.05, 39.1) * mm, "mid": v(4.22, 39.76) * mm, "end": v(7.3, 40.74) * mm});
            skArc(sketch, "E257", {"start": v(7.3, 40.74) * mm, "mid": v(11.1, 42.3) * mm, "end": v(14.81, 44.05) * mm});
            skArc(sketch, "E258", {"start": v(14.81, 44.05) * mm, "mid": v(21.86, 48.1) * mm, "end": v(28.42, 52.91) * mm});
            skArc(sketch, "E259", {"start": v(28.42, 52.91) * mm, "mid": v(35.27, 58.99) * mm, "end": v(41.62, 65.57) * mm});
            skArc(sketch, "E260", {"start": v(41.62, 65.57) * mm, "mid": v(47.4, 72.58) * mm, "end": v(52.6, 80.02) * mm});
            skArc(sketch, "E261", {"start": v(52.6, 80.02) * mm, "mid": v(56.5, 86.92) * mm, "end": v(59.58, 94.23) * mm});
            skArc(sketch, "E262", {"start": v(59.58, 94.23) * mm, "mid": v(60.52, 97.08) * mm, "end": v(61.37, 99.97) * mm});
            skArc(sketch, "E263", {"start": v(61.37, 99.97) * mm, "mid": v(61.74, 101.84) * mm, "end": v(61.87, 103.74) * mm});
            skArc(sketch, "E264", {"start": v(61.87, 103.74) * mm, "mid": v(61.72, 105.18) * mm, "end": v(61.27, 106.56) * mm});
            skArc(sketch, "E265", {"start": v(61.27, 106.56) * mm, "mid": v(60.52, 107.88) * mm, "end": v(59.55, 109.05) * mm});
            skArc(sketch, "E266", {"start": v(59.55, 109.05) * mm, "mid": v(58.55, 109.93) * mm, "end": v(57.45, 110.68) * mm});
            skArc(sketch, "E267", {"start": v(57.45, 110.68) * mm, "mid": v(56.48, 111.1) * mm, "end": v(55.44, 111.26) * mm});
            skArc(sketch, "E268", {"start": v(55.44, 111.26) * mm, "mid": v(54, 111.2) * mm, "end": v(52.58, 110.97) * mm});
            skArc(sketch, "E269", {"start": v(52.58, 110.97) * mm, "mid": v(49.54, 110.22) * mm, "end": v(46.5, 109.42) * mm});
            skSolve(sketch);
        }
        {
            var Q0;
            Q0=qSketchRegion(id+"F3",true);
            var Q1;
            Q1=sQuery(id+"F3.wireOp",EDGE,"c928f899-12af-4b01-b412-b3b7da3d830f");
            var Q2;
            Q2=sQuery(id+"F3.wireOp",EDGE,"b69f99c7-a6d0-4d1b-8752-9e82ab4c99ec");
            extrude(context, id + "F4", {"entities" : qUnion([Q0]), "operationType" : NewBodyOperationType.ADD, "surfaceEntities" : qUnion([Q1, Q2]), "depth" : 350 * mm});
        }
        {
            var Q0;
            Q0=makeQuery(id+"F4.opExtrude","SWEPT_BODY",BODY,{"disambiguationData":[OSD([sQuery(id+"F3.wireOp",EDGE,"15c6da4e-992d-4824-9d20-70d2d6be9970"),sQuery(id+"F3.wireOp",EDGE,"268c69ec-46be-456f-85eb-69decc32fe39"),sQuery(id+"F3.wireOp",EDGE,"1d386307-6059-4203-bca6-0c1cec3c82e1"),sQuery(id+"F3.wireOp",EDGE,"7d7c66d2-f869-427f-806b-ad436cacd60e"),sQuery(id+"F3.wireOp",EDGE,"1db91850-860e-493f-a3af-7a0f3f1512ae"),sQuery(id+"F3.wireOp",EDGE,"2c65f23b-9f03-4f6f-ab37-de452af29e3c"),sQuery(id+"F3.wireOp",EDGE,"ba006cbc-bbd7-44d9-84cc-9cde0967c280"),sQuery(id+"F3.wireOp",EDGE,"ae950208-c781-4a25-8fcf-ffe59b9085ff"),sQuery(id+"F3.wireOp",EDGE,"3cce0944-c62d-4831-9b9d-d1a418d328b4"),sQuery(id+"F3.wireOp",EDGE,"9edc5e7d-16c0-40c4-98ad-6b91d5df0e78"),sQuery(id+"F3.wireOp",EDGE,"aa452f44-44a2-4c64-bff5-a2a639df00db"),sQuery(id+"F3.wireOp",EDGE,"16259f99-ce20-4b7b-81e1-fa0909c03eb4"),sQuery(id+"F3.wireOp",EDGE,"79895566-a943-429d-b257-d76af3645bdf"),sQuery(id+"F3.wireOp",EDGE,"a85490ef-f17e-45c8-b92b-28215162778a"),sQuery(id+"F3.wireOp",EDGE,"322f1036-a6fd-4992-ab69-5919540af7a6"),sQuery(id+"F3.wireOp",EDGE,"0a87ff38-4ab4-4140-b3c3-2d7501d9f3b1"),sQuery(id+"F3.wireOp",EDGE,"a6e7bdf2-ef3e-49d4-9b3c-e34f5a41e0c4"),sQuery(id+"F3.wireOp",EDGE,"3e588790-576f-47c1-9730-f5e27fa1e8f9"),sQuery(id+"F3.wireOp",EDGE,"ce3739ef-15fd-4754-ad9c-ccf511a9a8fb"),sQuery(id+"F3.wireOp",EDGE,"201134a3-66f3-4a3f-aa9b-76948966efc0"),sQuery(id+"F3.wireOp",EDGE,"65b511ea-0759-428d-8070-88e1f521d8ea"),sQuery(id+"F3.wireOp",EDGE,"c37cddb6-5cf8-4891-aff4-7191a72080b9"),sQuery(id+"F3.wireOp",EDGE,"52a43dbd-e952-43e1-be3d-d70e107260e6"),sQuery(id+"F3.wireOp",EDGE,"08c1271f-f5c3-4f26-be27-7f5e21217dff"),sQuery(id+"F3.wireOp",EDGE,"59a09f58-0503-4180-962a-e04db21f0da8"),sQuery(id+"F3.wireOp",EDGE,"e56a4626-e956-42c3-bb5d-cd9dae1ca801"),sQuery(id+"F3.wireOp",EDGE,"5ff5d55f-af90-49eb-8040-353101557de8"),sQuery(id+"F3.wireOp",EDGE,"0ed7430b-e164-4f56-8af9-4534524aa7c0"),sQuery(id+"F3.wireOp",EDGE,"b5610a6e-b6bb-43e3-9a8d-d3d7c5f0098b"),sQuery(id+"F3.wireOp",EDGE,"1d417af8-88ad-47c2-a4e2-6fec82bd6695"),sQuery(id+"F3.wireOp",EDGE,"778ae99a-956a-4ddb-8078-d9bc57f9fc8e"),sQuery(id+"F3.wireOp",EDGE,"5b19af09-f144-446e-9dfa-8766819c9efd"),sQuery(id+"F3.wireOp",EDGE,"028339f6-0475-4a57-af8d-550e32ad7466"),sQuery(id+"F3.wireOp",EDGE,"d5ae35b6-d210-433a-92c8-e92622696872"),sQuery(id+"F3.wireOp",EDGE,"16a2e606-2caa-4876-9ffa-8f08c4ff3a37"),sQuery(id+"F3.wireOp",EDGE,"5b90b144-be56-4de7-a9dd-c1e0336acbe3"),sQuery(id+"F3.wireOp",EDGE,"5912d126-c5fc-41e4-bfb8-b4fefc52ca72"),sQuery(id+"F3.wireOp",EDGE,"2e96ce95-bd3e-4f27-a7f8-b62cf5efe954"),sQuery(id+"F3.wireOp",EDGE,"ecb4e259-1207-4dd0-bc3c-87c6506cc3a5"),sQuery(id+"F3.wireOp",EDGE,"105fb72e-4d79-4204-af2f-b3b26f5eb8d1"),sQuery(id+"F3.wireOp",EDGE,"fa59b598-df54-48c6-bb8f-c5f7618c69d0"),sQuery(id+"F3.wireOp",EDGE,"a6beef0d-f124-47ac-b957-e6cd3057a354"),sQuery(id+"F3.wireOp",EDGE,"7c3eaf53-dcb7-43b1-ad18-80ff953eb59e"),sQuery(id+"F3.wireOp",EDGE,"281fe206-104f-408f-94b6-be79f12604c9")])]});
            var Q1;
            Q1=makeQuery(id+"F4.opExtrude","SWEPT_BODY",BODY,{"disambiguationData":[OSD([sQuery(id+"F3.wireOp",EDGE,"58f6206a-5554-41d4-8cf7-6e0b4724a469"),sQuery(id+"F3.wireOp",EDGE,"85dabe77-b6aa-43d5-a519-64383616f71e"),sQuery(id+"F3.wireOp",EDGE,"4b679fe6-9e11-497d-b8fd-14ca14e49ddd"),sQuery(id+"F3.wireOp",EDGE,"51de25f6-d59e-4805-a327-1fd7e38869c8"),sQuery(id+"F3.wireOp",EDGE,"d47977fb-70d3-4df8-bc35-66fcc0e556e0"),sQuery(id+"F3.wireOp",EDGE,"235006b0-8f14-4ca2-82f0-f96b6b8c4766"),sQuery(id+"F3.wireOp",EDGE,"0fc7acd6-1c1d-47a8-ba12-62eb658d35ca"),sQuery(id+"F3.wireOp",EDGE,"883fa5e3-ca4c-4ce6-a249-4debf538fe24"),sQuery(id+"F3.wireOp",EDGE,"1da09ed1-22d9-43a1-a655-8acff5d61309"),sQuery(id+"F3.wireOp",EDGE,"32654a82-a09a-444f-bf73-45f818f0f235"),sQuery(id+"F3.wireOp",EDGE,"a398fd80-a0a9-4724-ba0e-1a7a000baa92"),sQuery(id+"F3.wireOp",EDGE,"f39f97c8-53f5-4046-9905-b28daecd4f10"),sQuery(id+"F3.wireOp",EDGE,"2484d883-0ec2-4c7d-9023-165ebbef226c"),sQuery(id+"F3.wireOp",EDGE,"f026d96f-3d32-4113-a1c9-3545f5cdbe4a"),sQuery(id+"F3.wireOp",EDGE,"974fee18-719e-4620-aace-d3676da2011b"),sQuery(id+"F3.wireOp",EDGE,"0c5766d2-a026-45af-bffd-0d1f783d5157"),sQuery(id+"F3.wireOp",EDGE,"5da13fee-9c04-45d8-805f-c7a03dde2383"),sQuery(id+"F3.wireOp",EDGE,"dbea32a3-85bd-4957-aef2-b6fe64a02f6b"),sQuery(id+"F3.wireOp",EDGE,"fba134ea-bf40-4191-ad8f-cc6b2b040a97"),sQuery(id+"F3.wireOp",EDGE,"0c19e200-7cd5-4fcb-83ed-261bd7936bc7"),sQuery(id+"F3.wireOp",EDGE,"246b843b-ea86-44e5-9cb9-335e6677b61d"),sQuery(id+"F3.wireOp",EDGE,"c1b3c9bc-1eb4-4c9b-99c8-0cebed89395a"),sQuery(id+"F3.wireOp",EDGE,"f93eebc3-1447-4029-8362-91325193ac2b"),sQuery(id+"F3.wireOp",EDGE,"bf86b12d-53a9-4c19-abaa-b1e658933ceb"),sQuery(id+"F3.wireOp",EDGE,"89646a71-1a60-4e14-b80a-74fb601d0855"),sQuery(id+"F3.wireOp",EDGE,"7b03dcde-0a52-4f3c-80e9-110d1d805e93"),sQuery(id+"F3.wireOp",EDGE,"83e8d1f3-8820-485b-8b6d-3ecd79124883"),sQuery(id+"F3.wireOp",EDGE,"ec7b56eb-ca95-44fd-a774-e9b7f9d3f50d"),sQuery(id+"F3.wireOp",EDGE,"31861aa6-cfd1-43ce-a7c5-bacfb7e2a30f"),sQuery(id+"F3.wireOp",EDGE,"fa3de647-1dd9-4141-982b-74ae8d07851d"),sQuery(id+"F3.wireOp",EDGE,"75d7c1c5-761c-4178-bfd4-4f469045899b"),sQuery(id+"F3.wireOp",EDGE,"4b3d7518-bd5d-4ecc-b2c5-d8dd665de4f4"),sQuery(id+"F3.wireOp",EDGE,"3be2682d-01bd-4f31-9cde-9df16a01e4a9"),sQuery(id+"F3.wireOp",EDGE,"72d3c7a9-2794-46eb-9b0d-6c526cc1b9a3"),sQuery(id+"F3.wireOp",EDGE,"0137e336-6b26-4f8d-b9ad-47ce1aa9eb31"),sQuery(id+"F3.wireOp",EDGE,"96000e4a-2d86-4b9f-af7d-a1c875cc048c"),sQuery(id+"F3.wireOp",EDGE,"139c5a79-9c0f-4e15-b57f-4c09662495a3"),sQuery(id+"F3.wireOp",EDGE,"8ea04d8b-b3da-46bb-9742-d8cba6b23bda"),sQuery(id+"F3.wireOp",EDGE,"b352b580-467e-481c-88ac-6217b8462947"),sQuery(id+"F3.wireOp",EDGE,"2503a493-1722-4539-8d54-7329fc0b116a"),sQuery(id+"F3.wireOp",EDGE,"a0615e06-0a48-4c65-8818-f0f693937022"),sQuery(id+"F3.wireOp",EDGE,"08389002-1ce8-438a-b5a4-698ca33590c2"),sQuery(id+"F3.wireOp",EDGE,"1756e4aa-c30a-461e-962c-81ee35d31e55"),sQuery(id+"F3.wireOp",EDGE,"5f84c249-07ea-4efb-9be3-ca494937f772"),sQuery(id+"F3.wireOp",EDGE,"cbefd041-b54f-4587-87b6-437b2290d1fc"),sQuery(id+"F3.wireOp",EDGE,"d44f58d4-f1a7-4aec-b016-8e7f1e498aeb"),sQuery(id+"F3.wireOp",EDGE,"0a5be90b-7545-44ea-9f2d-c726a5a2121c"),sQuery(id+"F3.wireOp",EDGE,"0cfaa442-d102-4580-8ef6-489f2aa1e6b3")])]});
            var Q2;
            Q2=makeQuery(id+"F4.opExtrude","SWEPT_BODY",BODY,{"disambiguationData":[OSD([sQuery(id+"F3.wireOp",EDGE,"9cc7aec6-4d94-4577-ab6c-32f5aa316238"),sQuery(id+"F3.wireOp",EDGE,"5ab2d840-4a32-405a-8c4b-a8126e3e1bc1"),sQuery(id+"F3.wireOp",EDGE,"56de48b4-9620-4637-8196-310e2641530f"),sQuery(id+"F3.wireOp",EDGE,"55327826-e64b-4830-85f2-3f22d36f43b5"),sQuery(id+"F3.wireOp",EDGE,"0245b46f-a639-4a95-8ca3-1568736ceed2"),sQuery(id+"F3.wireOp",EDGE,"9bd8a002-6ca7-4c84-8984-a620eefad103"),sQuery(id+"F3.wireOp",EDGE,"d4736c5e-da0b-46a0-ba9d-17ae07bb2b66"),sQuery(id+"F3.wireOp",EDGE,"125695b8-77e6-4e99-8f78-5f8fae1a0c71"),sQuery(id+"F3.wireOp",EDGE,"c9f25b10-a495-4684-8f25-8f255fabab6e"),sQuery(id+"F3.wireOp",EDGE,"0dbee67a-2ab6-4abb-ae16-0fe64d623848"),sQuery(id+"F3.wireOp",EDGE,"92c08d8e-ed2e-41a3-9c1a-b5ddaf8a0bf1"),sQuery(id+"F3.wireOp",EDGE,"00fabb15-0c1e-492e-85c1-17390e5b12bc"),sQuery(id+"F3.wireOp",EDGE,"065a9352-dddb-4e3f-b02a-444c867b75fe"),sQuery(id+"F3.wireOp",EDGE,"ef206bb6-e4f2-4189-9fc7-a7823c329ad6"),sQuery(id+"F3.wireOp",EDGE,"7199cbbe-c9bf-4cb9-b928-2ff8a84eb09e"),sQuery(id+"F3.wireOp",EDGE,"17bf9ed1-b881-4f74-816d-3511b6b328c7"),sQuery(id+"F3.wireOp",EDGE,"e5b615d0-4193-495d-b285-bd69ae30f000"),sQuery(id+"F3.wireOp",EDGE,"cfeaf62f-6be1-426b-9732-01e1a667be7e"),sQuery(id+"F3.wireOp",EDGE,"ac56344b-5ee6-4fa5-8e47-65b2a4ea3a01"),sQuery(id+"F3.wireOp",EDGE,"45b5fa53-15fd-43a0-91b0-943cc3286fc9")])]});
            var Q3;
            Q3=makeQuery(id+"F4.opExtrude","SWEPT_BODY",BODY,{"disambiguationData":[OSD([sQuery(id+"F3.wireOp",EDGE,"7bdfe37d-9957-4663-8239-5490fd3220d9"),sQuery(id+"F3.wireOp",EDGE,"6a91314f-c002-4565-bbf8-bb9f29165fb8"),sQuery(id+"F3.wireOp",EDGE,"b69f99c7-a6d0-4d1b-8752-9e82ab4c99ec"),sQuery(id+"F3.wireOp",EDGE,"c928f899-12af-4b01-b412-b3b7da3d830f"),sQuery(id+"F3.wireOp",EDGE,"ffa58721-cdd5-406d-be26-d96f7a050df4"),sQuery(id+"F3.wireOp",EDGE,"02fc7fb8-293b-44ff-ab78-63506d0aedb9"),sQuery(id+"F3.wireOp",EDGE,"147fb6cb-2565-4fb5-9280-6afbf9eef36b"),sQuery(id+"F3.wireOp",EDGE,"2cee3704-4124-415a-b391-31af1cf305d7"),sQuery(id+"F3.wireOp",EDGE,"32b2fb71-03c8-4978-9d95-2b5aaf044d0d"),sQuery(id+"F3.wireOp",EDGE,"e5d05796-7d6c-4350-8a4e-d55f5ade2f77"),sQuery(id+"F3.wireOp",EDGE,"77b1164c-8dd4-4680-b616-ac151a422eb2"),sQuery(id+"F3.wireOp",EDGE,"ec0798b8-0fbb-49ea-9766-39d2ee0936b0"),sQuery(id+"F3.wireOp",EDGE,"c4af6478-2a03-47a6-862f-c0c71886b8a3"),sQuery(id+"F3.wireOp",EDGE,"1912a38f-fa28-45c6-ab33-84cac2787056"),sQuery(id+"F3.wireOp",EDGE,"5d79fa95-f66d-4d2b-923b-4d54735f1fbd"),sQuery(id+"F3.wireOp",EDGE,"2db7aef4-a710-4bcf-9c1c-a8a87719953d"),sQuery(id+"F3.wireOp",EDGE,"183449de-345c-4115-9bca-43a403e62dbd"),sQuery(id+"F3.wireOp",EDGE,"e3ac8c9b-cab5-44b0-ad81-0e2b680c384a"),sQuery(id+"F3.wireOp",EDGE,"92e85db6-f458-41f6-a9a1-1e1a1a7e7809"),sQuery(id+"F3.wireOp",EDGE,"f0dbb46f-43a9-447b-9c75-8dfc9b95470d"),sQuery(id+"F3.wireOp",EDGE,"4b73f5f6-f769-4414-bdba-7d253e58fff4"),sQuery(id+"F3.wireOp",EDGE,"a88669dc-35b3-46bb-964f-c9bf6c4ab898"),sQuery(id+"F3.wireOp",EDGE,"2c559bae-f38f-4377-91e6-3c9de70acf11"),sQuery(id+"F3.wireOp",EDGE,"c1caf99b-adaa-42fe-a319-8cbcd819cf89"),sQuery(id+"F3.wireOp",EDGE,"54b04dd4-0ec4-4956-b19c-1141095738e3"),sQuery(id+"F3.wireOp",EDGE,"098f7a84-b7b8-4879-b21a-5c38879e4110"),sQuery(id+"F3.wireOp",EDGE,"b406a8e6-a226-4f3d-ac30-e4d06e4dac62"),sQuery(id+"F3.wireOp",EDGE,"36f95d1d-68ce-4231-ad71-3960c85e5915"),sQuery(id+"F3.wireOp",EDGE,"dc12cad8-2eed-454e-aa74-30099b1c9064"),sQuery(id+"F3.wireOp",EDGE,"4c78a4fd-cd81-43d6-85d6-6e4d3fbc1e98"),sQuery(id+"F3.wireOp",EDGE,"ee9e30de-787b-4e8f-b425-43a8e9289f81"),sQuery(id+"F3.wireOp",EDGE,"2518a3a4-c96b-4463-8704-0b71c65c60d2"),sQuery(id+"F3.wireOp",EDGE,"c9129a67-398c-4e37-92cb-2d54ff2e2e82"),sQuery(id+"F3.wireOp",EDGE,"d429d547-9f5b-42c6-bcca-effad2fa908f"),sQuery(id+"F3.wireOp",EDGE,"99d16e94-b2b3-43d5-9c7b-7bd463994dcb"),sQuery(id+"F3.wireOp",EDGE,"32993909-9a70-47ee-9097-89fff220f839"),sQuery(id+"F3.wireOp",EDGE,"6eabbeed-9496-4825-b168-63782a34f495"),sQuery(id+"F3.wireOp",EDGE,"f74987e3-8e60-4a5b-857f-839ae8aaf0cf"),sQuery(id+"F3.wireOp",EDGE,"1c218c86-035d-4441-93c0-9621d3297c3a"),sQuery(id+"F3.wireOp",EDGE,"0133f513-4b11-4cc4-b075-4625e9591e41"),sQuery(id+"F3.wireOp",EDGE,"fe921ad4-a8f5-4772-9aeb-350aca2e8948"),sQuery(id+"F3.wireOp",EDGE,"bfde0a4f-3cec-4f8e-8a23-dd1441b34c2b"),sQuery(id+"F3.wireOp",EDGE,"b41521ff-c5df-4b64-83ed-5e7635cf4438"),sQuery(id+"F3.wireOp",EDGE,"ed692599-6bbb-4379-8e89-ea326a0a0f87"),sQuery(id+"F3.wireOp",EDGE,"a98451c0-d76c-436e-99f9-a3fe9c8430a4"),sQuery(id+"F3.wireOp",EDGE,"561965b2-3050-4f49-9305-d98a2b852bbe"),sQuery(id+"F3.wireOp",EDGE,"e13dfa59-48e6-4b4e-94b9-1fc5254b0f2e"),sQuery(id+"F3.wireOp",EDGE,"0354e106-253a-4bfa-b5b7-b09cd0f2f6c0"),sQuery(id+"F3.wireOp",EDGE,"8df1dcc8-d00a-4777-85fd-8af8e9830bd1"),sQuery(id+"F3.wireOp",EDGE,"26ce3762-0d1a-4b81-9a23-debcfc24da1c"),sQuery(id+"F3.wireOp",EDGE,"3e900f8f-3ffb-4e32-b536-61fea2f3e30a"),sQuery(id+"F3.wireOp",EDGE,"4a1b5445-5559-461f-b6f1-b4cd9b95ea10")])]});
            var Q4;
            Q4=makeQuery(id+"F1.opRevolve","SWEPT_BODY",BODY,{"disambiguationData":[OSD([sQuery(id+"F0.wireOp",EDGE,"E0"),sQuery(id+"F0.wireOp",EDGE,"E1")])]});
            var Q5;
            Q5=qCreatedBy(makeId("Origin.pointOp"),VERTEX);
            transform(context, id + "F5", {"entities" : qUnion([Q0, Q1, Q2, Q3, Q4]), "transformType" : TransformType.SCALE_UNIFORMLY, "scale" : 0.03, "scalePoint" : qUnion([Q5]), "makeCopy" : false});
        }
        {
            var Q0;
            Q0=qCreatedBy(makeId("Top.planeOp"),FACE);
            var sketch = newSketch(context, id + "F6", { "sketchPlane" : qUnion([Q0])});
            skLineSegment(sketch, "E270", {"start": v(0, 15) * mm, "end": v(0, -15) * mm});
            skArc(sketch, "E271", {"start": v(0, 15) * mm, "mid": v(-15, 0) * mm, "end": v(0, -15) * mm});
            skArc(sketch, "E272", {"start": v(0, 10.25) * mm, "mid": v(-10.25, 0) * mm, "end": v(0, -10.25) * mm});
            skArc(sketch, "E273", {"start": v(0, 7) * mm, "mid": v(-7, 0) * mm, "end": v(0, -7) * mm});
            skSolve(sketch);
        }
        {
            var Q0;
            {var subQ0=sQuery(id+"F6.wireOp",EDGE,"E271");Q0=makeQuery(id+"F6.imprint","IMPRINT",FACE,{"disambiguationData":[TD([[makeQuery(id+"F6.imprint","IMPRINT",EDGE,{"derivedFrom":subQ0}),1.0]])]});}
            var Q1;
            {var subQ0=sQuery(id+"F6.wireOp",EDGE,"E273");Q1=makeQuery(id+"F6.imprint","IMPRINT",FACE,{"disambiguationData":[TD([[makeQuery(id+"F6.imprint","IMPRINT",EDGE,{"derivedFrom":subQ0}),1.0]])]});}
            var Q2;
            Q2=sQuery(id+"F6.wireOp",EDGE,"E270");
            revolve(context, id + "F7", {"operationType" : NewBodyOperationType.REMOVE, "entities" : qUnion([Q0, Q1]), "axis" : qUnion([Q2]), "revolveType" : RevolveType.FULL});
        }
        {
            var Q0;
            Q0=makeQuery(id+"F1.opRevolve","SWEPT_BODY",BODY,{"disambiguationData":[OSD([sQuery(id+"F0.wireOp",EDGE,"E0"),sQuery(id+"F0.wireOp",EDGE,"E1")])]});
            var Q1;
            Q1=sQuery(id+"F0.wireOp",VERTEX,"E1.center");
            transform(context, id + "F8", {"entities" : qUnion([Q0]), "transformType" : TransformType.SCALE_UNIFORMLY, "scale" : 1.4, "scalePoint" : qUnion([Q1]), "makeCopy" : false});
        }
        {
            var Q0;
            Q0=qCreatedBy(makeId("Front.planeOp"),FACE);
            var sketch = newSketch(context, id + "F9", { "sketchPlane" : qUnion([Q0])});
            skCircle(sketch, "E274", {"center": v(0, -5.12) * mm, "radius": 2 * mm});
            skSolve(sketch);
        }
        {
            var Q0;
            Q0=qSketchRegion(id+"F9",true);
            extrude(context, id + "F10", {"entities" : qUnion([Q0]), "operationType" : NewBodyOperationType.REMOVE, "oppositeDirection" : true, "depth" : 25 * mm});
        }
    });
